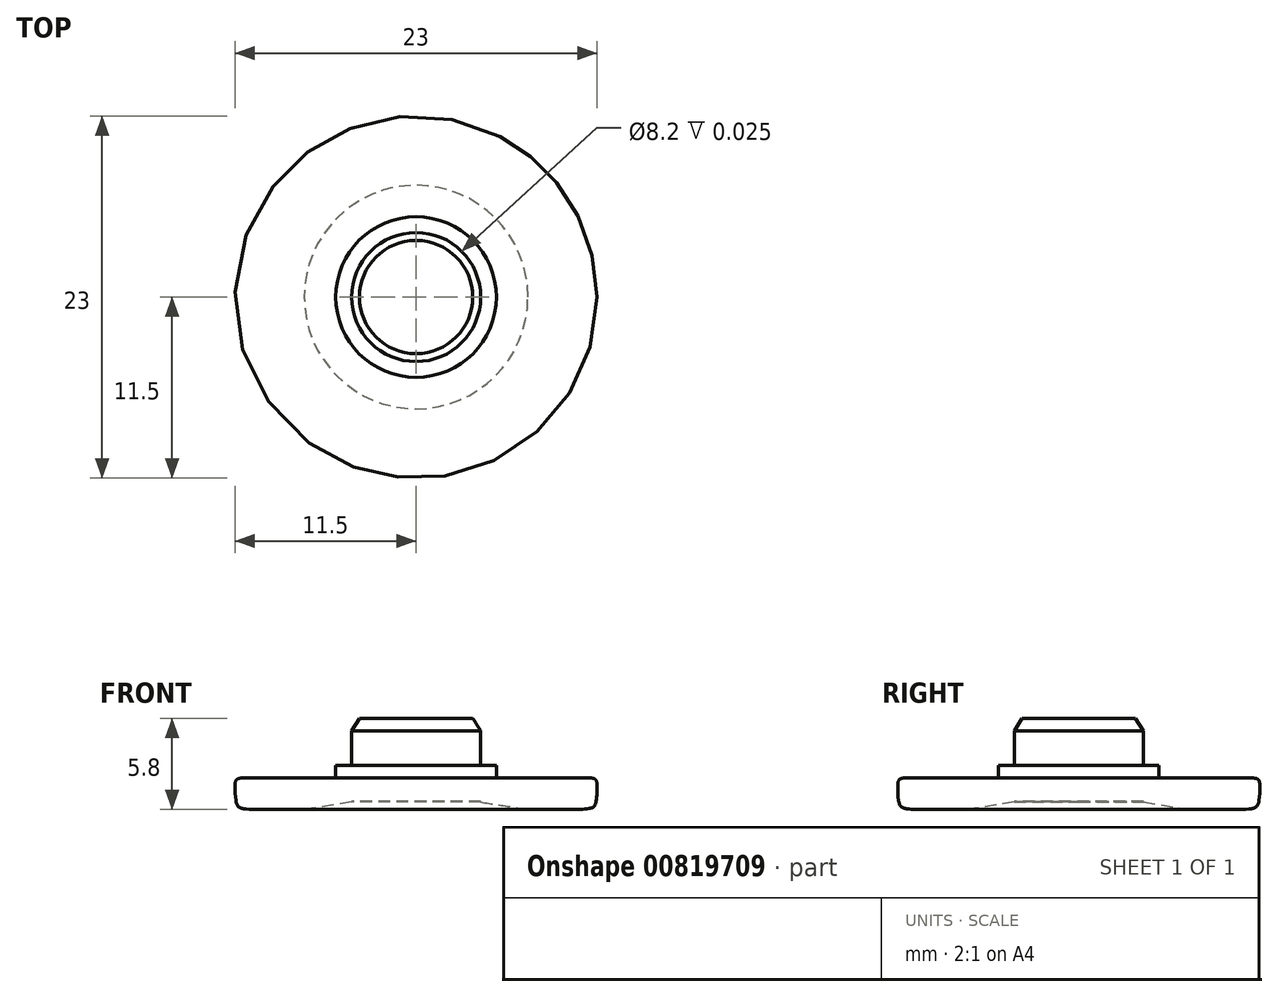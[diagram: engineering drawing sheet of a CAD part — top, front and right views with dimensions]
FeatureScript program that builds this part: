
annotation { "Feature Type Name" : "Feature", "Feature Type Description" : "" }
export const myFeature = defineFeature(function(context is Context, id is Id, definition is map)
    precondition{}
    {
        {
            var Q0;
            Q0=qCreatedBy(makeId("Top.planeOp"),FACE);
            var sketch = newSketch(context, id + "F0", { "sketchPlane" : qUnion([Q0])});
            skCircle(sketch, "E0", {"center": v(0, 0) * mm, "radius": 11.5 * mm});
            skCircle(sketch, "E1", {"center": v(0, 0) * mm, "radius": 4.1 * mm});
            skCircle(sketch, "E2", {"center": v(0, 0) * mm, "radius": 5.1 * mm});
            skSolve(sketch);
        }
        {
            var Q0;
            Q0=makeQuery(id+"F0.imprint","IMPRINT",FACE,{"disambiguationData":[TD([[makeQuery(id+"F0.imprint","IMPRINT",EDGE,{"derivedFrom":sQuery(id+"F0.wireOp",EDGE,"E1")}),1.0]])]});
            extrude(context, id + "F1", {"entities" : qUnion([Q0]), "depth" : 5.8 * mm, "offsetDistance" : 25 * mm, "hasSecondDirection" : true, "secondDirectionOppositeDirection" : true, "secondDirectionDepth" : -.5 * mm});
        }
        {
            var Q0;
            Q0=makeQuery(id+"F0.imprint","IMPRINT",FACE,{"disambiguationData":[TD([[makeQuery(id+"F0.imprint","IMPRINT",EDGE,{"derivedFrom":sQuery(id+"F0.wireOp",EDGE,"E1")}),-1.0]])]});
            extrude(context, id + "F2", {"entities" : qUnion([Q0]), "operationType" : NewBodyOperationType.ADD, "depth" : 2.8 * mm, "offsetDistance" : 25 * mm});
        }
        {
            var Q0;
            Q0=makeQuery(id+"F0.imprint","IMPRINT",FACE,{"disambiguationData":[TD([[makeQuery(id+"F0.imprint","IMPRINT",EDGE,{"derivedFrom":sQuery(id+"F0.wireOp",EDGE,"E0")}),1.0]])]});
            extrude(context, id + "F3", {"entities" : qUnion([Q0]), "operationType" : NewBodyOperationType.ADD, "depth" : 2 * mm, "offsetDistance" : 25 * mm});
        }
        {
            var Q0;
            Q0=makeQuery(id+"F1.opExtrude","CAP_EDGE",EDGE,{"disambiguationData":[OSD([sQuery(id+"F0.wireOp",EDGE,"E1")])],"isStart":false});
            chamfer(context, id + "F4", {"entities" : qUnion([Q0]), "chamferType" : ChamferType.TWO_OFFSETS, "width1" : .5 * mm, "oppositeDirection" : false, "width2" : .8 * mm, "tangentPropagation" : true});
        }
        {
            var Q0;
            Q0=makeQuery(id+"F3.opExtrude","CAP_EDGE",EDGE,{"disambiguationData":[OSD([sQuery(id+"F0.wireOp",EDGE,"E0")])],"isStart":true});
            fillet(context, id + "F5", {"entities" : qUnion([Q0]), "radius" : 2 * mm, "tangentPropagation" : true, "rho" : .8, "crossSection" : FilletCrossSection.CONIC, "allowEdgeOverflow" : false});
        }
        {
            var Q0;
            {var subQ0=sQuery(id+"F0.wireOp",EDGE,"E2");Q0=makeQuery(id+"F3.boolean.opBoolean","MERGE",FACE,{"derivedFrom":[makeQuery(id+"F2.opExtrude","CAP_FACE",FACE,{"disambiguationData":[OSD([sQuery(id+"F0.wireOp",EDGE,"E1"),subQ0])],"isStart":true}),makeQuery(id+"F3.opExtrude","CAP_FACE",FACE,{"disambiguationData":[OSD([sQuery(id+"F0.wireOp",EDGE,"E0"),subQ0])],"isStart":true})]});}
            chamfer(context, id + "F6", {"entities" : qUnion([Q0]), "chamferType" : ChamferType.OFFSET_ANGLE, "width" : 3 * mm, "oppositeDirection" : false, "angle" : 9 * degree});
        }
        {
            var Q0;
            {var subQ0=sQuery(id+"F0.wireOp",EDGE,"E0");Q0=makeQuery(id+"F5.opFillet","BLEND_EDGE",EDGE,{"blendedFrom":[makeQuery(id+"F3.opExtrude","CAP_EDGE",EDGE,{"disambiguationData":[OSD([subQ0])],"isStart":true}),makeQuery(id+"F3.opExtrude","CAP_FACE",FACE,{"disambiguationData":[OSD([subQ0,sQuery(id+"F0.wireOp",EDGE,"E2")])],"isStart":false})],"blendedInto":[makeQuery(id+"F3.opExtrude","CAP_FACE",FACE,{"disambiguationData":[OSD([subQ0,sQuery(id+"F0.wireOp",EDGE,"E2")])],"isStart":false})]});}
            fillet(context, id + "F7", {"entities" : qUnion([Q0]), "radius" : .5 * mm, "tangentPropagation" : true, "rho" : .6, "crossSection" : FilletCrossSection.CONIC, "allowEdgeOverflow" : false});
        }
    });
